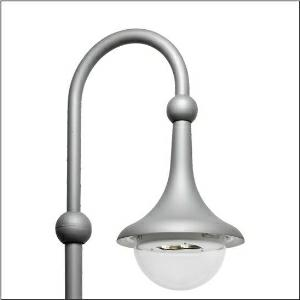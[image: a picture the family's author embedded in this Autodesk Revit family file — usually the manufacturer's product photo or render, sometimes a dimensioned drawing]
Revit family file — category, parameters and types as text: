
# Revit family: grosse_glocke_iq___st1_2a_5xa1565k1f108_5d30
name_source: partatom
category: Lighting Fixtures
units: mm (PartAtom-declared; Revit-internal decimal feet)

## family parameters
Cut with Voids When Loaded = No
Host = Face
Light Source = No
Part Type = Normal
Room Calculation Point = No
Round Connector Dimension = Use Diameter
Shared = No

## types (1)
- --- (1 x LED, 5420 lm, 34.3 W, 4000K)
    Apparent Load = 34 VA
    CIE Flux Codes = 28 66 95 100 100
    Color Rendering = 70
    Color Temperature = 4000K
    Default Elevation = 1800 mm
    Description = Large Bell iQ, mast luminaire, primary light control with 3 zone facetted reflector, of plastic, silver coated, primary optical cover: enclosure, of PMMA, transparent, light distribution: ST1.2a, light emission: direct distribution, primary light characteristic: asymmetric, installation type: suspended mounting, High Power LED, rated luminous flux: 5.420lm, luminous efficacy: 158lm/W, light colour: 740, colour temperature: 4000K, control gear: iQ Street-Remote, control: optimised constant luminous flux control (CLO 2.0), Desk-Remote (wireless, voltage-free reading and setting of iQ features in the workshop via application-optimized NFC function/RFID function), Light-Fading, Smart-Wire, Night-Set, Lumen-Switch, Temp-Guard, Auto-Match, Street-Remote, pre-setting: logarithmic dimming characteristic, mains connection: 230..240V, AC, 50/60Hz, start of lifetime: 34W, end of service life: 38W, reduction: 16W, luminaire housing, bell-shaped, of glass-fibre reinforced polyester, coated, Siteco® metallic grey (DB 702S), please order curved mast extension separately, diameter: 530mm, height: 695mm, mounting height: 4..6m, protection rating (complete): IP54, insulation class (complete): insulation class II (safety insulation), certification: CE, ENEC, VDE, impact resistance: IK08, standard-compliant lighting for roads and squares, packaging unit: 1 piece

Light Distribution: ST1.2a
    Height = 695 mm
    Lamp = 1 x LED
    Lamp Light Flux = 5420 lm
    Lamp Power = 34.3 W
    Lamp count = 1
    Length = 530 mm
    Luminous efficacy = 158 lm/W
    Manufacturer = Siteco
    ModVariant = No
    Model = 5XA1565K1F108
    Number of Poles = 1
    OnlyDefault = Yes
    Power Factor = 1
    Product Name = Große Glocke iQ | ST1.2a
    Product group = mast luminaire | pylon annexe
    ProductGroupID = 6201
    Protection Class = Protection class II
    Protection Degree = IP 54
    RLX_Detail_Level = 1
    RLX_Emergency_Light_Flux = 0 lm
    RLX_Emergency_Type = 0
    RLX_Emergency_Type_DB = No
    RlxData = <blob elided: 85365 chars, md5=4e4e71fa>
    Socket = socket
    Standby Power = 0 W
    System Light Flux = 5420 lm
    System Power = 34 W
    Type Comments = factory setting: luminous flux: 100 % | dim-lin: 254 | 640 mA
    Type Image = l_1347688.jpg
    URL = http://relux.com
    VarID = @adj_059778
    Voltage = 0 V
    Weight = 0.00 kg
    Width = 0 mm  [stored 0 ft]

note: [stored X ft] marks values corroborated as IEEE doubles in the binary element streams (Revit-internal decimal feet)

## geometry (parser evidence)
native form markers: Blend x4, Sweep x11
no freeform markers — native parametric forms only
